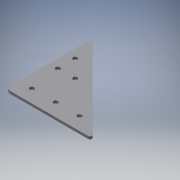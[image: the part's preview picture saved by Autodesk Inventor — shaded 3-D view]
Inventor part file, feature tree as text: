
AUTODESK INVENTOR PART (.ipt)
format: ipt  version: 2017 (Build 210142000, 142)  size: 389,120 bytes
history: native  units: mm
features: sketch x2, extrude x1, hole x1, projected_geometry x1
ambient origin geometry x8: Origin, YZ Plane, XZ Plane, XY Plane, X Axis, Y Axis, Z Axis, Center Point
bodies: Solid1 (feature_tree)
feature tree (5):
  extrude  "Extrusion1"  [1 undecoded]
  hole  "Hole1"  [1 undecoded]
  sketch  "Sketch1"  dims[d0=3.0mm d1=0.0mm]
  sketch  "Sketch2"  dims[d2=5.2mm d3=6.0mm d4=4.0mm d5=2.0mm d6=90.0deg d7=8.0mm d8=20.594885mm]
  projected_geometry  "Projected Loop1"
note: 2 required parameter values undecoded (feature->parameter linkage not recoverable at this tier; creation-order binding heuristic only, values carry confidence <= 0.55)
